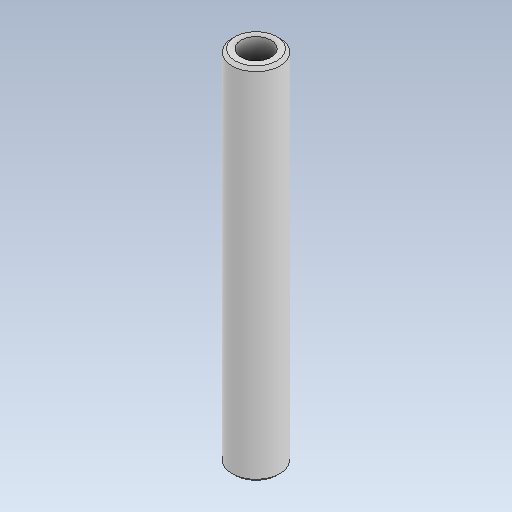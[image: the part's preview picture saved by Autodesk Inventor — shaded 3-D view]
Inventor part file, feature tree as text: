
AUTODESK INVENTOR PART (.ipt)
format: ipt  version: 2020 (Build 240168000, 168)  size: 101,376 bytes
history: native  units: mm
features: extrude x1, chamfer x1, sketch x1
ambient origin geometry x8: Origin, YZ Plane, XZ Plane, XY Plane, X Axis, Y Axis, Z Axis, Center Point
bodies: Solid1 (feature_tree)
feature tree (3):
  extrude  "Extrusion1"  Depth=60.0mm
  chamfer  "Chamfer1"  Distance=60.0mm
  sketch  "Sketch1"  dims[d0=8.0mm d1=5.0mm d2=60.0mm d3=0.0mm d4=0.5mm d5=2.0mm d6=45.0deg]
